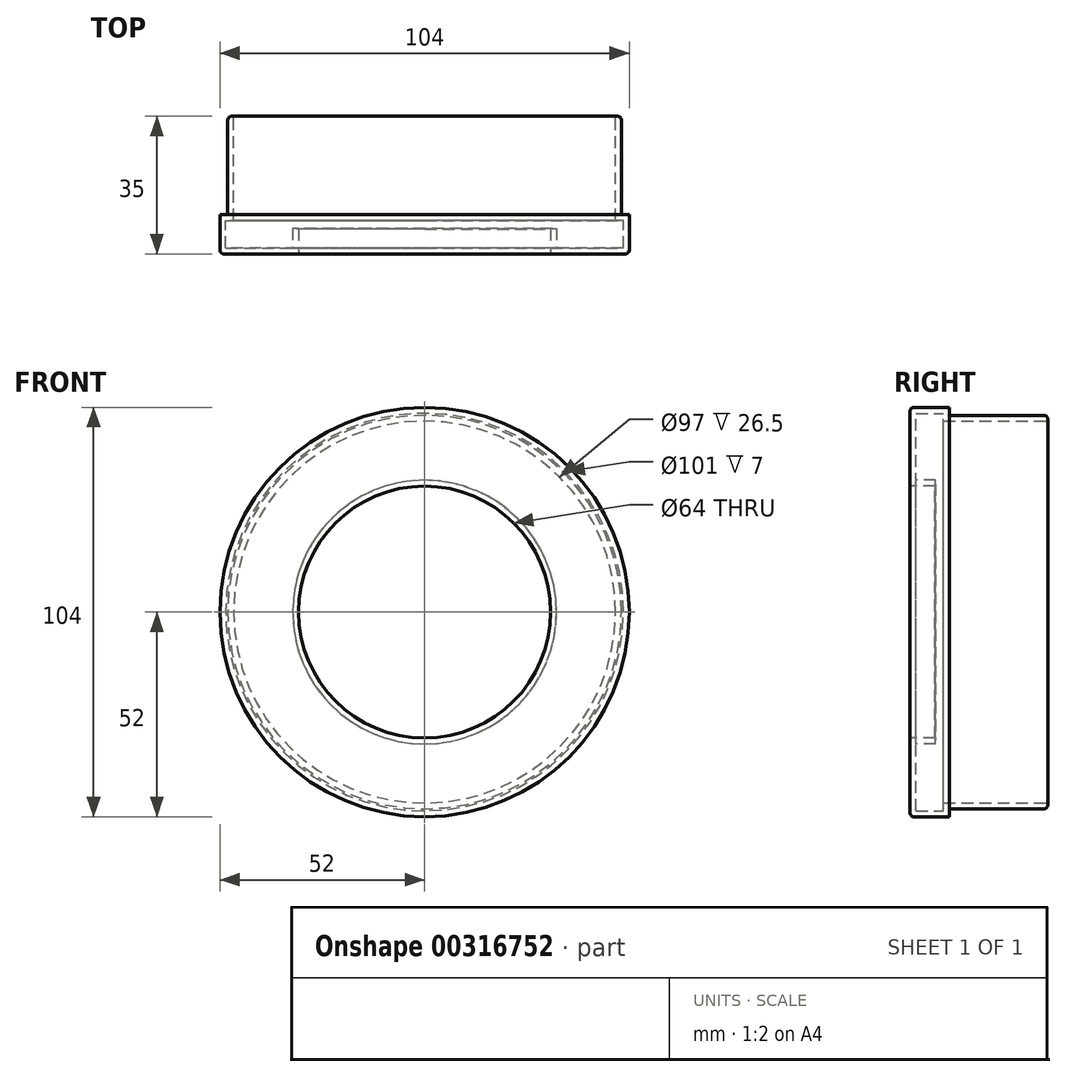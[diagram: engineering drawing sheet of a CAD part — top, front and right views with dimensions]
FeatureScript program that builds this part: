
annotation { "Feature Type Name" : "Feature", "Feature Type Description" : "" }
export const myFeature = defineFeature(function(context is Context, id is Id, definition is map)
    precondition{}
    {
        {
            var Q0;
            Q0=qCreatedBy(makeId("Front.planeOp"),FACE);
            var sketch = newSketch(context, id + "F0", { "sketchPlane" : qUnion([Q0])});
            skCircle(sketch, "E0", {"center": v(0, 0) * mm, "radius": 50 * mm});
            skSolve(sketch);
        }
        {
            var Q0;
            Q0=makeQuery(id+"F0.imprint","IMPRINT",FACE,{"disambiguationData":[TD([[makeQuery(id+"F0.imprint","IMPRINT",EDGE,{"derivedFrom":sQuery(id+"F0.wireOp",EDGE,"E0")}),1.0]])]});
            extrude(context, id + "F1", {"entities" : qUnion([Q0]), "depth" : 25 * mm});
        }
        {
            var Q0;
            Q0=makeQuery(id+"F1.opExtrude","CAP_FACE",FACE,{"disambiguationData":[OSD([sQuery(id+"F0.wireOp",EDGE,"E0")])],"isStart":false});
            var sketch = newSketch(context, id + "F2", { "sketchPlane" : qUnion([Q0])});
            skCircle(sketch, "E1", {"center": v(0, 0) * mm, "radius": 52 * mm});
            skSolve(sketch);
        }
        {
            var Q0;
            Q0=makeQuery(id+"F2.imprint","IMPRINT",FACE,{"disambiguationData":[TD([[makeQuery(id+"F2.imprint","IMPRINT",EDGE,{"derivedFrom":sQuery(id+"F2.wireOp",EDGE,"E1")}),1.0]])]});
            var Q1;
            Q1=makeQuery(id+"F2.imprint","IMPRINT",FACE,{"disambiguationData":[TD([[makeQuery(id+"F2.imprint","IMPRINT",EDGE,{"derivedFrom":makeQuery(id+"F1.opExtrude","CAP_EDGE",EDGE,{"disambiguationData":[OSD([sQuery(id+"F0.wireOp",EDGE,"E0")])],"isStart":false})}),1.0]])]});
            extrude(context, id + "F3", {"entities" : qUnion([Q0, Q1]), "operationType" : NewBodyOperationType.ADD, "depth" : 10 * mm});
        }
        {
            var Q0;
            Q0=makeQuery(id+"F3.opExtrude","CAP_EDGE",EDGE,{"disambiguationData":[OSD([sQuery(id+"F2.wireOp",EDGE,"E1")])],"isStart":false});
            var Q1;
            Q1=makeQuery(id+"F1.opExtrude","CAP_EDGE",EDGE,{"disambiguationData":[OSD([sQuery(id+"F0.wireOp",EDGE,"E0")])],"isStart":true});
            fillet(context, id + "F4", {"entities" : qUnion([Q0, Q1]), "radius" : 1 * mm, "tangentPropagation" : true, "allowEdgeOverflow" : false});
        }
        {
            var Q0;
            Q0=makeQuery(id+"F1.opExtrude","CAP_FACE",FACE,{"disambiguationData":[OSD([sQuery(id+"F0.wireOp",EDGE,"E0")])],"isStart":true});
            shell(context, id + "F5", {"entities" : qUnion([Q0]), "thickness" : 1.5 * mm});
        }
        {
            var Q0;
            {var subQ0=sQuery(id+"F2.wireOp",EDGE,"E1");Q0=makeQuery(id+"F5.opShell","OFFSET_FACE",FACE,{"disambiguationData":[OSD([subQ0]),TDD([makeQuery(id+"F3.opExtrude","CAP_FACE",FACE,{"disambiguationData":[OSD([subQ0])],"isStart":false})])]});}
            var sketch = newSketch(context, id + "F6", { "sketchPlane" : qUnion([Q0])});
            skCircle(sketch, "E2", {"center": v(0, 0) * mm, "radius": 31.5 * mm});
            skCircle(sketch, "E3", {"center": v(0, 0) * mm, "radius": 33.5 * mm});
            skSolve(sketch);
        }
        {
            var Q0;
            Q0=makeQuery(id+"F6.imprint","IMPRINT",FACE,{"disambiguationData":[TD([[makeQuery(id+"F6.imprint","IMPRINT",EDGE,{"derivedFrom":sQuery(id+"F6.wireOp",EDGE,"E2")}),-1.0]])]});
            extrude(context, id + "F7", {"entities" : qUnion([Q0]), "operationType" : NewBodyOperationType.ADD, "depth" : 5 * mm});
        }
        {
            var Q0;
            Q0=makeQuery(id+"F7.opExtrude","CAP_EDGE",EDGE,{"disambiguationData":[OSD([sQuery(id+"F6.wireOp",EDGE,"E2")])],"isStart":false});
            fillet(context, id + "F8", {"entities" : qUnion([Q0]), "radius" : 1 * mm, "tangentPropagation" : true, "allowEdgeOverflow" : false});
        }
        {
            var Q0;
            Q0=makeQuery(id+"F3.opExtrude","CAP_FACE",FACE,{"disambiguationData":[OSD([sQuery(id+"F2.wireOp",EDGE,"E1")])],"isStart":false});
            var sketch = newSketch(context, id + "F9", { "sketchPlane" : qUnion([Q0])});
            skCircle(sketch, "E4", {"center": v(0, 0) * mm, "radius": 32 * mm});
            skSolve(sketch);
        }
        {
            var Q0;
            Q0=makeQuery(id+"F9.imprint","IMPRINT",FACE,{"disambiguationData":[TD([[makeQuery(id+"F9.imprint","IMPRINT",EDGE,{"derivedFrom":sQuery(id+"F9.wireOp",EDGE,"E4")}),1.0]])]});
            extrude(context, id + "F10", {"entities" : qUnion([Q0]), "operationType" : NewBodyOperationType.REMOVE, "oppositeDirection" : true, "depth" : 25 * mm});
        }
    });
